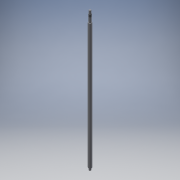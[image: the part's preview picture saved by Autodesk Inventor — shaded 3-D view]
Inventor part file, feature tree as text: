
AUTODESK INVENTOR PART (.ipt)
format: ipt  version: 2018 (Build 220112000, 112)  size: 124,416 bytes
history: native  units: mm
features: extrude x6, sketch x6, other x1, thread x1, chamfer x1
ambient origin geometry x8: Origin, YZ Plane, XZ Plane, XY Plane, X Axis, Y Axis, Z Axis, Center Point
bodies: Body1 (feature_tree)
feature tree (15):
  other  "Sólido1"
  extrude  "Extrusão1"  Depth=635.0mm TaperAngle=0.0deg
  extrude  "Extrusão2"  Depth=39.0mm TaperAngle=0.0deg
  extrude  "Extrusão3"  Depth=15.0mm TaperAngle=0.0deg
  extrude  "Extrusão4"  Depth=9.15mm TaperAngle=0.0deg
  extrude  "Extrusão5"  Depth=1.15mm TaperAngle=0.0deg
  extrude  "Extrusão6"  Depth=1.85mm TaperAngle=0.0deg
  thread  "Rosca1"  [1 undecoded]
  chamfer  "Chanfro1"  Distance=0.5mm Angle=45.0deg
  sketch  "Esboço1"  dims[d0=16.0mm d1=635.0mm d2=0.0mm]
  sketch  "Esboço2"  dims[d3=12.0mm d4=39.0mm d5=0.0mm]
  sketch  "Esboço3"  dims[d6=10.0mm d7=15.0mm d8=0.0mm]
  sketch  "Esboço4"  dims[d9=10.0mm d10=9.15mm d11=0.0mm]
  sketch  "Esboço5"  dims[d12=9.0mm d13=1.15mm d14=0.0mm]
  sketch  "Esboço6"  dims[d15=10.0mm d16=1.85mm d17=0.0mm d18=14.0mm d19=0.0mm d20=0.5mm d21=2.0mm d22=45.0deg]
note: 1 required parameter value undecoded (feature->parameter linkage not recoverable at this tier; creation-order binding heuristic only, values carry confidence <= 0.55)
